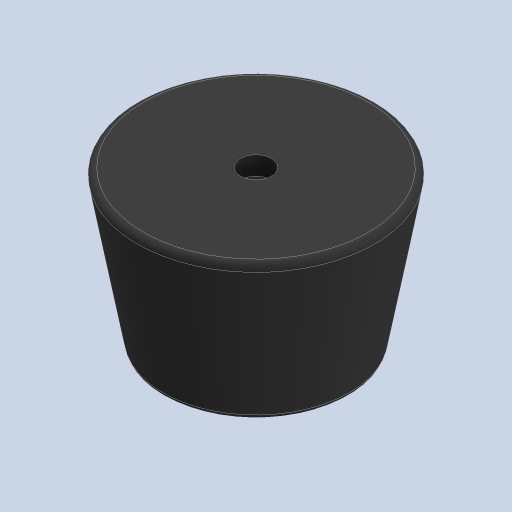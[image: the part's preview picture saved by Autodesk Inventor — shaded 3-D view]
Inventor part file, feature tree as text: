
AUTODESK INVENTOR PART (.ipt)
format: ipt  version: 2023 (Build 270158000, 158)  size: 162,816 bytes
history: native  units: mm
features: revolve x1, sketch x1
ambient origin geometry x8: Origin, YZ Plane, XZ Plane, XY Plane, X Axis, Y Axis, Z Axis, Center Point
bodies: Body1 (feature_tree)
feature tree (2):
  revolve  "Revolution1"  [1 undecoded]
  sketch  "Sketch5"  dims[d21=17.0mm d22=12.0mm d23=15.0mm d24=13.0mm d25=2.5mm d26=25.0mm d27=3.0mm d28=1.0mm d29=1.0mm d30=90.0deg]
note: 1 required parameter value undecoded (feature->parameter linkage not recoverable at this tier; creation-order binding heuristic only, values carry confidence <= 0.55)
